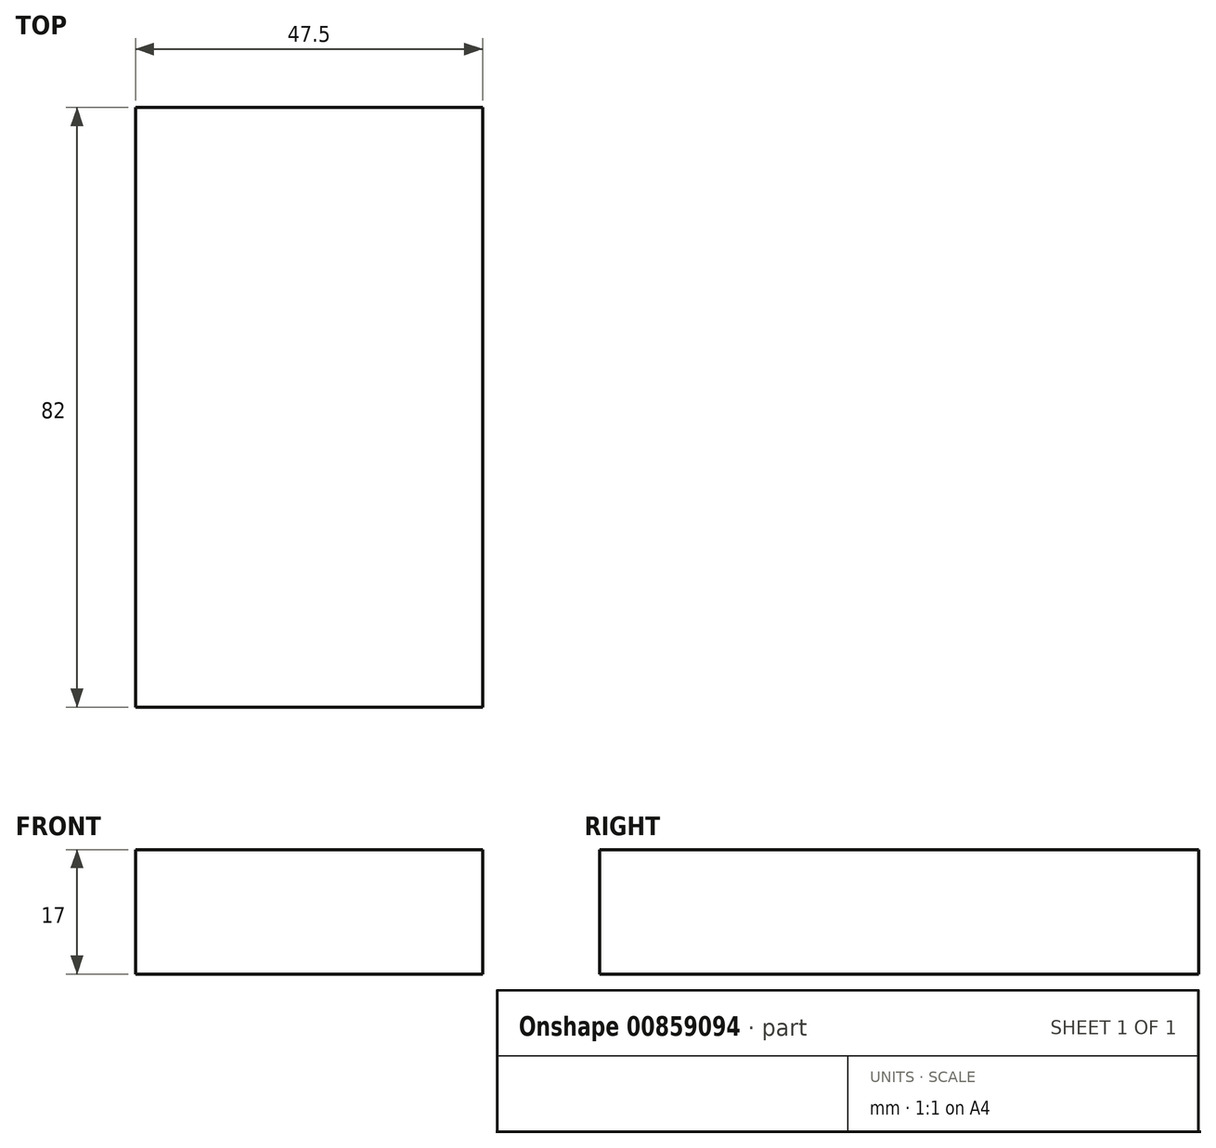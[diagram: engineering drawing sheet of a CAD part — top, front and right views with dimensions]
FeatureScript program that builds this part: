
annotation { "Feature Type Name" : "Feature", "Feature Type Description" : "" }
export const myFeature = defineFeature(function(context is Context, id is Id, definition is map)
    precondition{}
    {
        {
            var Q0;
            Q0=qCreatedBy(makeId("Top.planeOp"),FACE);
            var sketch = newSketch(context, id + "F0", { "sketchPlane" : qUnion([Q0])});
            skLineSegment(sketch, "E0.bottom", {"start": v(23.75, -41) * mm, "end": v(-23.75, -41) * mm});
            skLineSegment(sketch, "E0.top", {"start": v(23.75, 41) * mm, "end": v(-23.75, 41) * mm});
            skLineSegment(sketch, "E0.left", {"start": v(23.75, -41) * mm, "end": v(23.75, 41) * mm});
            skLineSegment(sketch, "E0.right", {"start": v(-23.75, -41) * mm, "end": v(-23.75, 41) * mm});
            skPoint(sketch, "E0.middle", {"position": v(0, 0) * mm});
            skSolve(sketch);
        }
        {
            var Q0;
            Q0 = qSketchRegion(id + "F0", true);
            extrude(context, id + "F1", {"entities" : qUnion([Q0]), "depth" : 17 * mm, "offsetDistance" : 25 * mm});
        }
    });
